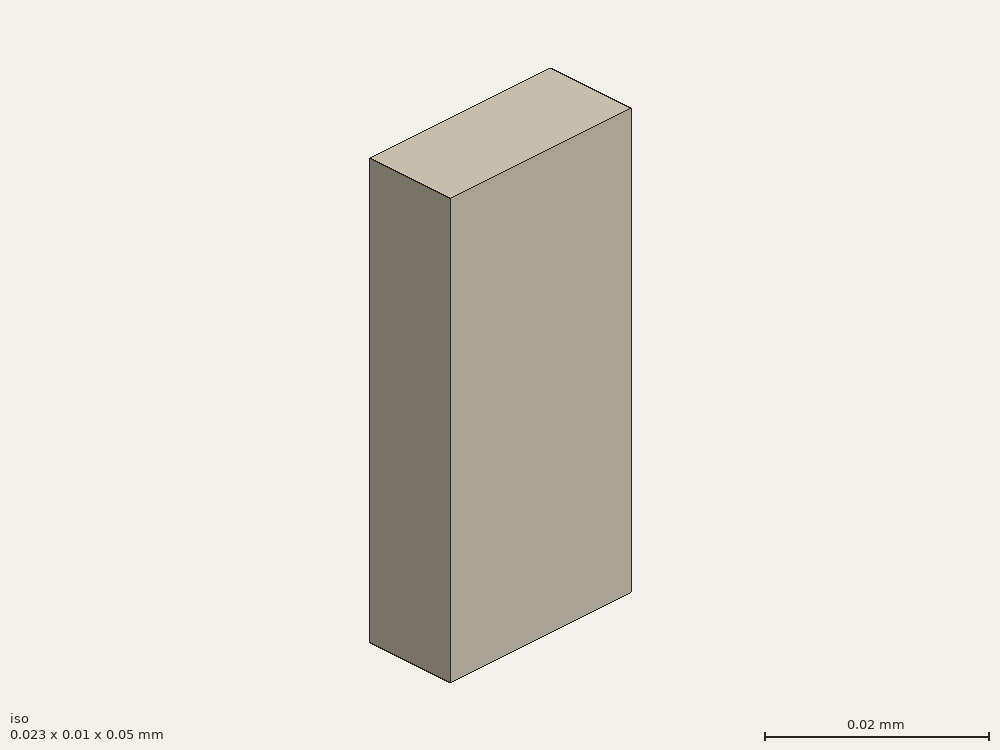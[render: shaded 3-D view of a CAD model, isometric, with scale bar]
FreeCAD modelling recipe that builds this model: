
FCSTD DOCUMENT  (FreeCAD 0.21R33694 (Git))
Label: opened
License: All rights reserved
LicenseURL: http://en.wikipedia.org/wiki/All_rights_reserved
objects: Part::Part2DObjectPython×4, App::FeaturePython×3, Part::Extrusion×1, Part::FeaturePython×1
note: 6 computed .brp shape members not serialized (recipe doc carries the construction recipe); baked Part::Feature solids carry a one-line shape summary decoded from their .brp

FEATURE [Part::Part2DObjectPython] Rectangle  # Draft 2D object (typed FeaturePython)
  Area = 232.258
  ChamferSize = 0
  Columns = 1
  FilletRadius = 0
  Height = 10.16
  Length = 22.86
  MakeFace = true
  Placement = pos=(-11.43,-5.08,0) rot=(0,0,1;0rad)
  Rows = 1
FEATURE [Part::Extrusion] Extrude
  Base = -> Rectangle
  Dir = (0,0,1)
  DirMode = 2
  FaceMakerClass = Part::FaceMakerBullseye
  LengthFwd = 50
  LengthRev = 0
  Solid = false
  Symmetric = false
FEATURE [Part::FeaturePython] Clone  label="Extrude001"  # Draft clone (typed FeaturePython)
  AttacherType = Attacher::AttachEngine3D
  Fuse = false
  Objects = -> [Extrude]
  Scale = (0.001,0.001,0.001)
FEATURE [Part::Part2DObjectPython] Rectangle001  label="_Pport1"  # Draft 2D object (typed FeaturePython)
  Area = 0.000232258
  ChamferSize = 0
  Columns = 1
  FilletRadius = 0
  Height = 0.01016
  Length = 0.02286
  MakeFace = true
  Placement = pos=(-0.01143,-0.00508,0.05) rot=(0,0,1;0rad)
  Rows = 1
FEATURE [Part::Part2DObjectPython] Line  label="_Pv1"  # Draft 2D object (typed FeaturePython)
  Area = 0
  ChamferSize = 0
  Closed = false
  End = (-1.8e-15,0.00508,0.05)
  FilletRadius = 0
  Length = 0.01016
  MakeFace = true
  Placement = pos=(-0.011,-0.005,3e-15) rot=(0,0,1;0rad)
  Points = (2) [(0.011,-8e-05,0.05),(0.011,0.01008,0.05)]
  Start = (0,-0.00508,0.05)
  Subdivisions = 0
FEATURE [App::FeaturePython] Text  label="_S1(PV){port1}"  # WARN: FeaturePython — macro-defined, semantics opaque (R4)
  Placement = pos=(0.0413747,-0.017509,0) rot=(0,0,1;0rad)
  Text = .
FEATURE [App::FeaturePython] Text002  label="_L1(1,voltage){v1}"  # WARN: FeaturePython — macro-defined, semantics opaque (R4)
  Placement = pos=(0.0413747,-0.017509,0) rot=(0,0,1;0rad)
  Text = .
FEATURE [Part::Part2DObjectPython] Rectangle002  label="_Popen"  # Draft 2D object (typed FeaturePython)
  Area = 0.000232258
  ChamferSize = 0
  Columns = 1
  FilletRadius = 0
  Height = 0.01016
  Length = 0.02286
  MakeFace = true
  Placement = pos=(-0.01143,-0.00508,0) rot=(0,0,1;0rad)
  Rows = 1
FEATURE [App::FeaturePython] Text003  label="_Bopen(PMC){open}"  # WARN: FeaturePython — macro-defined, semantics opaque (R4)
  Placement = pos=(0.0413747,-0.017509,0) rot=(0,0,1;0rad)
  Text = .
